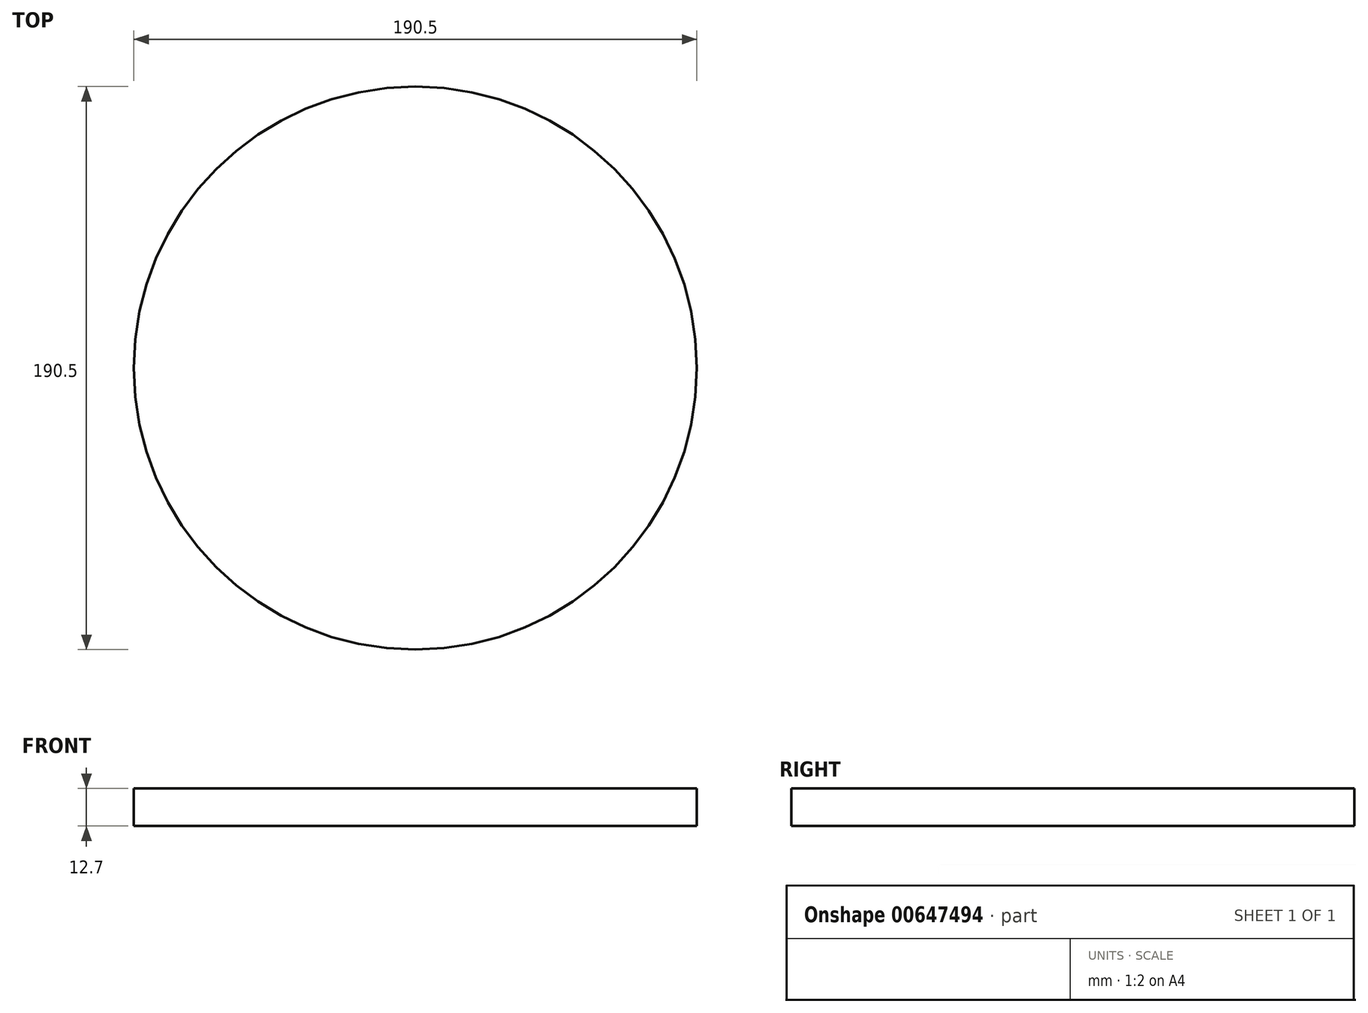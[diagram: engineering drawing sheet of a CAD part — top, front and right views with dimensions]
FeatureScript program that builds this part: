
annotation { "Feature Type Name" : "Feature", "Feature Type Description" : "" }
export const myFeature = defineFeature(function(context is Context, id is Id, definition is map)
    precondition{}
    {
        {
            var Q0;
            Q0=qCreatedBy(makeId("Top.planeOp"),FACE);
            var sketch = newSketch(context, id + "F0", { "sketchPlane" : qUnion([Q0])});
            skCircle(sketch, "E0", {"center": v(0, 0) * mm, "radius": 95.25 * mm});
            skSolve(sketch);
        }
        {
            var Q0;
            Q0=qSketchRegion(id+"F0",true);
            extrude(context, id + "F1", {"entities" : qUnion([Q0]), "depth" : 12.7 * mm});
        }
    });
